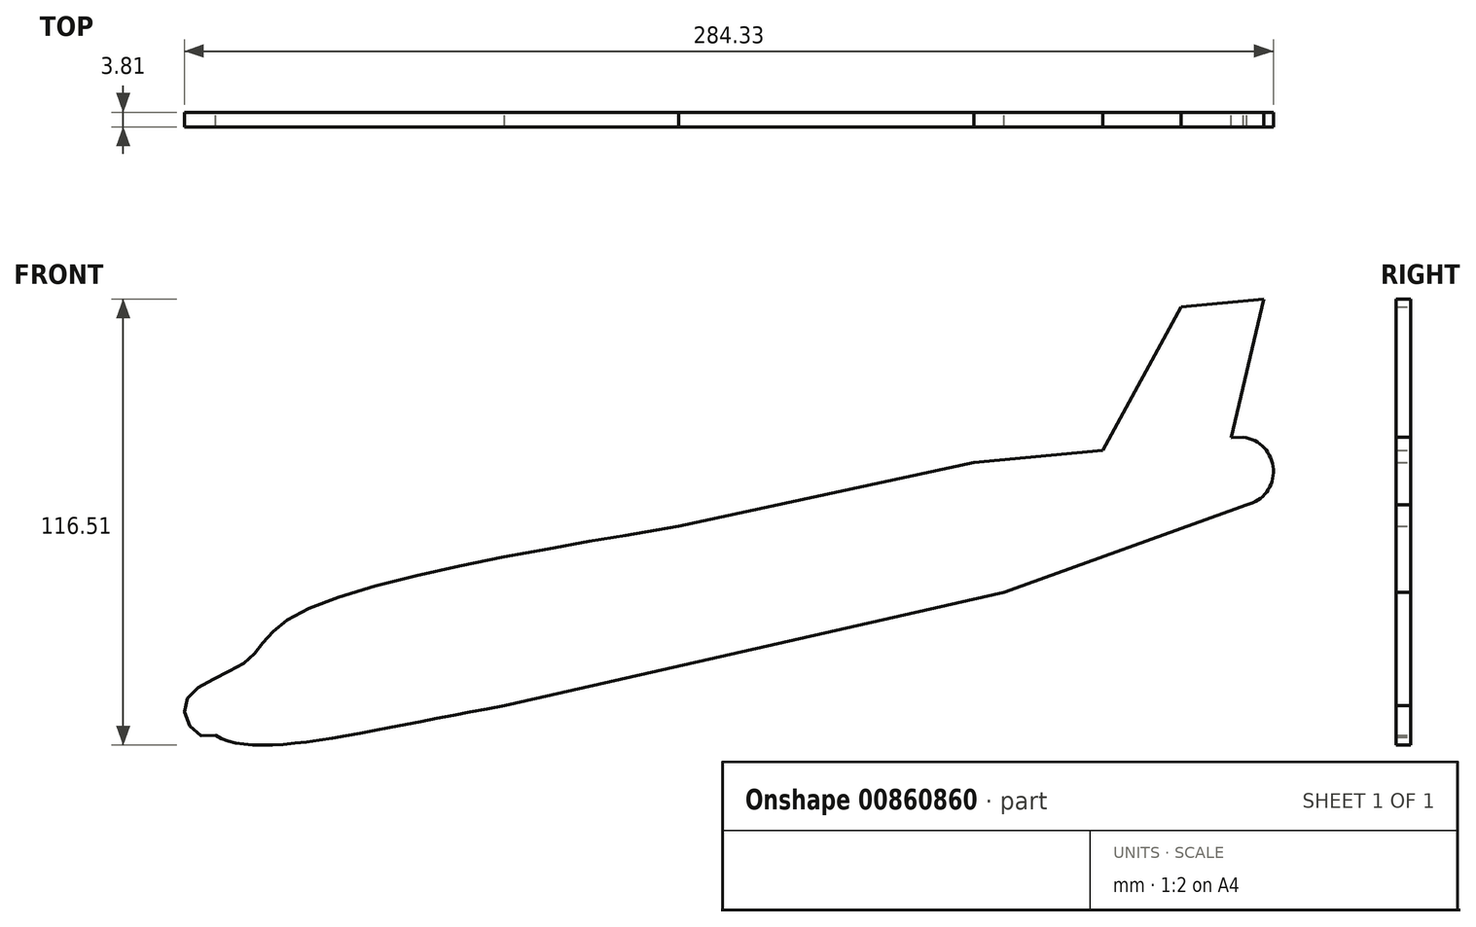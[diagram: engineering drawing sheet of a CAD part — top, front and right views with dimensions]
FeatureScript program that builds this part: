
annotation { "Feature Type Name" : "Feature", "Feature Type Description" : "" }
export const myFeature = defineFeature(function(context is Context, id is Id, definition is map)
    precondition{}
    {
        {
            var Q0;
            Q0=qCreatedBy(makeId("Front.planeOp"),FACE);
            var sketch = newSketch(context, id + "F0", { "sketchPlane" : qUnion([Q0])});
            skLineSegment(sketch, "E0", {"start": v(-26.33, 6.32) * mm, "end": v(50.8, 22.92) * mm});
            skLineSegment(sketch, "E1", {"start": v(-71.79, -40.63) * mm, "end": v(58.64, -11.06) * mm});
            skPoint(sketch, "E2.center.orphan", {"position": v(97.26, 13.98) * mm});
            skPoint(sketch, "E3.end.orphan", {"position": v(96.96, 15.28) * mm});
            skArc(sketch, "E4", {"start": v(122.04, 11.85) * mm, "mid": v(128.78, 22.63) * mm, "end": v(118, 29.36) * mm});
            skLineSegment(sketch, "E5", {"start": v(122.04, 11.85) * mm, "end": v(58.64, -11.06) * mm});
            skLineSegment(sketch, "E6", {"start": v(84.4, 26.14) * mm, "end": v(50.8, 22.92) * mm});
            skLineSegment(sketch, "E7", {"start": v(84.4, 26.14) * mm, "end": v(104.9, 63.5) * mm});
            skLineSegment(sketch, "E8", {"start": v(104.9, 63.5) * mm, "end": v(126.5, 65.58) * mm});
            skLineSegment(sketch, "E9", {"start": v(126.5, 65.58) * mm, "end": v(118, 29.36) * mm});
            skPoint(sketch, "E10.orphan", {"position": v(62.67, 35.2) * mm});
            skPoint(sketch, "E11.orphan", {"position": v(63.8, 52.7) * mm});
            skPoint(sketch, "E12.start.orphan", {"position": v(97.77, 50.52) * mm});
            skPoint(sketch, "E13.start.orphan", {"position": v(80.78, 51.62) * mm});
            skPoint(sketch, "E14.start.orphan", {"position": v(73.53, 30.67) * mm});
            skLineSegment(sketch, "E15", {"start": v(126.5, 65.58) * mm, "end": v(148.42, 56.12) * mm});
            skLineSegment(sketch, "E16", {"start": v(148.42, 56.12) * mm, "end": v(141.17, 30.58) * mm});
            skLineSegment(sketch, "E17", {"start": v(141.17, 30.58) * mm, "end": v(118, 29.36) * mm});
            skPoint(sketch, "E18.end.orphan", {"position": v(83.6, -33.08) * mm});
            skPoint(sketch, "E18.start.orphan", {"position": v(63.96, -34.12) * mm});
            skPoint(sketch, "E19.1.internal.orphan", {"position": v(-106.54, -46.68) * mm});
            skFitSpline(sketch, "E20", {"points": [v(-71.79, -40.63) * mm, v(-147.17, -48.4) * mm], "startDerivative": vector(-104.25, -18.17) * mm, "endDerivative": vector(-32.81, 20.5) * mm});
            skFitSpline(sketch, "E21", {"points": [v(-26.33, 6.32) * mm, v(-125.94, -16.68) * mm, v(-139.84, -29.49) * mm, v(-155.2, -40.37) * mm, v(-147.17, -48.4) * mm], "startDerivative": vector(-105.71, -20.11) * mm, "endDerivative": vector(94.64, 44.32) * mm});
            skLineSegment(sketch, "E22.0", {"start": v(-125.94, -16.68) * mm, "end": v(-26.33, 6.32) * mm, "construction": true});
            skLineSegment(sketch, "E23.0", {"start": v(96.96, 15.28) * mm, "end": v(120.02, 20.6) * mm, "construction": true});
            skLineSegment(sketch, "E24.0", {"start": v(63.96, -34.12) * mm, "end": v(50.8, 22.92) * mm, "construction": true});
            skLineSegment(sketch, "E25.0", {"start": v(122.04, 11.85) * mm, "end": v(118, 29.36) * mm, "construction": true});
            skLineSegment(sketch, "E26.0", {"start": v(83.6, -33.08) * mm, "end": v(63.8, 52.7) * mm, "construction": true});
            skLineSegment(sketch, "E27.0", {"start": v(97.26, 13.98) * mm, "end": v(96.96, 15.28) * mm, "construction": true});
            skSolve(sketch);
        }
        {
            var Q0;
            Q0=makeQuery(id+"F0.imprint","IMPRINT",FACE,{"disambiguationData":[TD([[makeQuery(id+"F0.imprint","IMPRINT",EDGE,{"derivedFrom":sQuery(id+"F0.wireOp",EDGE,"E0")}),-1.0]])]});
            extrude(context, id + "F1", {"entities" : qUnion([Q0]), "depth" : 3.8 * mm, "offsetDistance" : 25.4 * mm});
        }
    });
